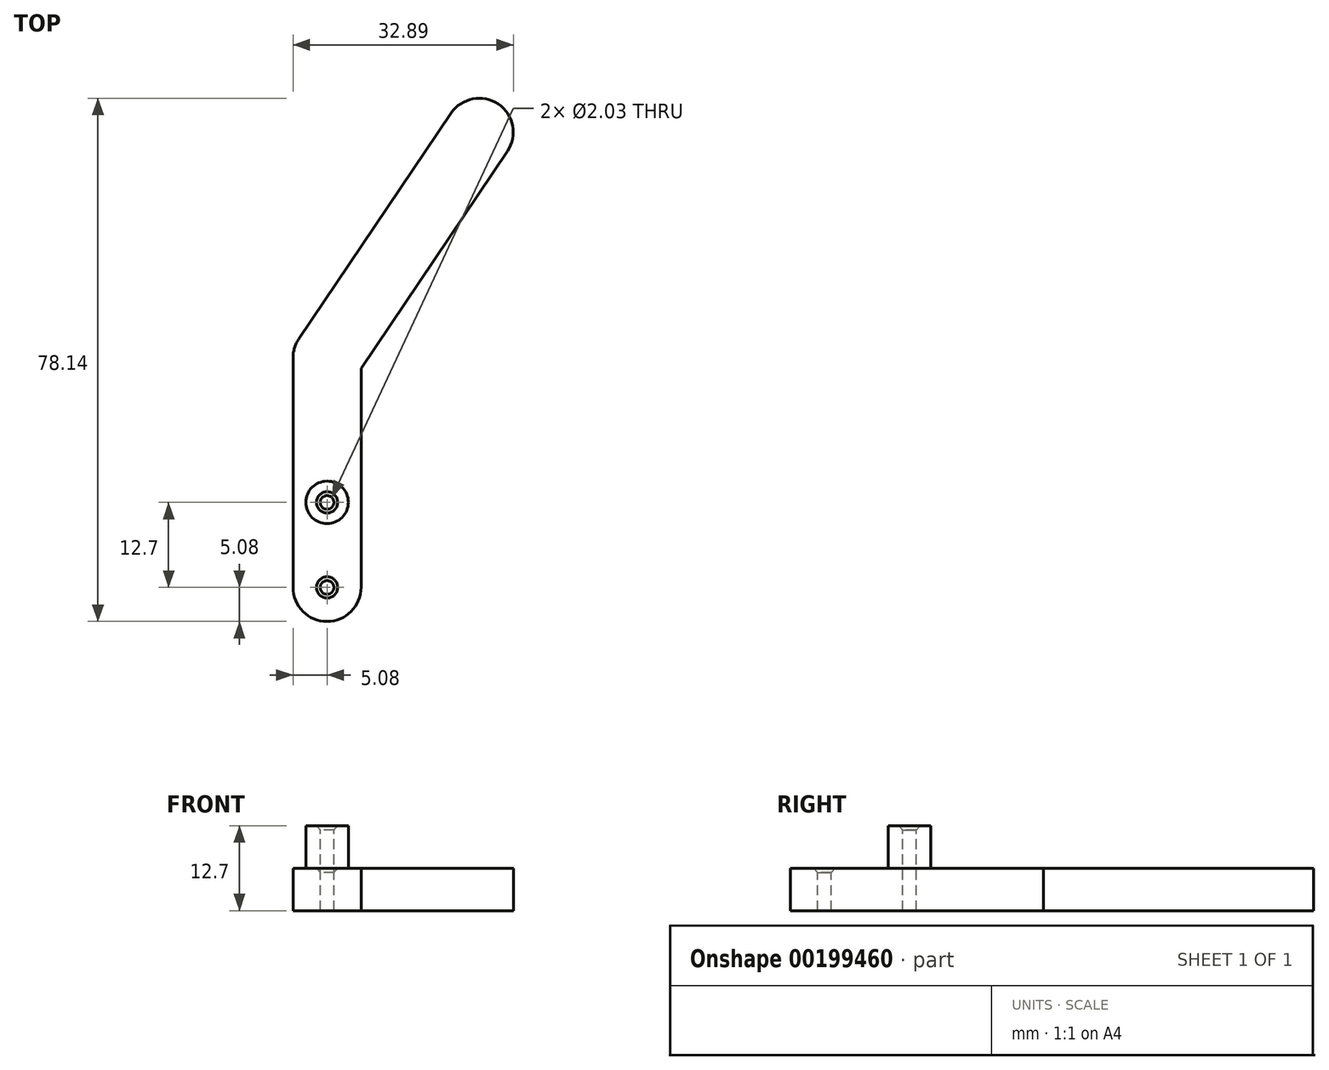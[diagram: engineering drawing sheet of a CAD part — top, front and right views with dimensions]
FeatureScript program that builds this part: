
annotation { "Feature Type Name" : "Feature", "Feature Type Description" : "" }
export const myFeature = defineFeature(function(context is Context, id is Id, definition is map)
    precondition{}
    {
        {
            var Q0;
            Q0=qCreatedBy(makeId("Top.planeOp"),FACE);
            var sketch = newSketch(context, id + "F0", { "sketchPlane" : qUnion([Q0])});
            skLineSegment(sketch, "E0", {"start": v(0, 0) * mm, "end": v(0, 12.7) * mm});
            skLineSegment(sketch, "E1", {"start": v(0, 12.7) * mm, "end": v(0, 34.3) * mm});
            skLineSegment(sketch, "E2", {"start": v(0, 34.3) * mm, "end": v(22.73, 67.98) * mm});
            skArc(sketch, "E3.0.startCap", {"start": v(4.21, 31.45) * mm, "mid": v(-2.84, 30.08) * mm, "end": v(-4.21, 37.13) * mm});
            skArc(sketch, "E3.0.endCap", {"start": v(18.51, 70.82) * mm, "mid": v(25.57, 72.2) * mm, "end": v(26.94, 65.14) * mm});
            skLineSegment(sketch, "E3.0.left", {"start": v(-4.21, 37.13) * mm, "end": v(18.51, 70.82) * mm});
            skLineSegment(sketch, "E3.0.right", {"start": v(4.21, 31.45) * mm, "end": v(26.94, 65.14) * mm});
            skArc(sketch, "E3.1.startCap", {"start": v(5.08, 12.7) * mm, "mid": v(0, 7.62) * mm, "end": v(-5.08, 12.7) * mm});
            skArc(sketch, "E3.1.endCap", {"start": v(-5.08, 34.3) * mm, "mid": v(0, 39.37) * mm, "end": v(5.08, 34.3) * mm});
            skLineSegment(sketch, "E3.1.left", {"start": v(-5.08, 12.7) * mm, "end": v(-5.08, 34.3) * mm});
            skLineSegment(sketch, "E3.1.right", {"start": v(5.08, 12.7) * mm, "end": v(5.08, 34.3) * mm});
            skArc(sketch, "E3.2.startCap", {"start": v(5.08, 0) * mm, "mid": v(0, -5.08) * mm, "end": v(-5.08, 0) * mm});
            skArc(sketch, "E3.2.endCap", {"start": v(-5.08, 12.7) * mm, "mid": v(0, 17.78) * mm, "end": v(5.08, 12.7) * mm});
            skLineSegment(sketch, "E3.2.left", {"start": v(-5.08, 0) * mm, "end": v(-5.08, 12.7) * mm});
            skLineSegment(sketch, "E3.2.right", {"start": v(5.08, 0) * mm, "end": v(5.08, 12.7) * mm});
            skSolve(sketch);
        }
        {
            var Q0;
            Q0 = qSketchRegion(id + "F0", true);
            extrude(context, id + "F1", {"entities" : qUnion([Q0]), "depth" : 6.35 * mm});
        }
        {
            var Q0;
            Q0=makeQuery(id+"F1.opExtrude","CAP_FACE",FACE,{"disambiguationData":[OSD([sQuery(id+"F0.wireOp",EDGE,"E3.0.endCap"),sQuery(id+"F0.wireOp",EDGE,"E3.0.left"),sQuery(id+"F0.wireOp",EDGE,"E3.0.right"),sQuery(id+"F0.wireOp",EDGE,"E3.1.endCap"),sQuery(id+"F0.wireOp",EDGE,"E3.1.left"),sQuery(id+"F0.wireOp",EDGE,"E3.1.right"),sQuery(id+"F0.wireOp",EDGE,"E3.2.startCap"),sQuery(id+"F0.wireOp",EDGE,"E3.2.left"),sQuery(id+"F0.wireOp",EDGE,"E3.2.right")])],"isStart":false});
            var sketch = newSketch(context, id + "F2", { "sketchPlane" : qUnion([Q0])});
            skCircle(sketch, "E4", {"center": v(0, 12.7) * mm, "radius": 3.18 * mm});
            skSolve(sketch);
        }
        {
            var Q0;
            Q0=makeQuery(id+"F2.imprint","IMPRINT",FACE,{"disambiguationData":[TD([[makeQuery(id+"F2.imprint","IMPRINT",EDGE,{"derivedFrom":sQuery(id+"F2.wireOp",EDGE,"E4")}),1.0]])]});
            extrude(context, id + "F3", {"entities" : qUnion([Q0]), "operationType" : NewBodyOperationType.ADD, "depth" : 6.35 * mm});
        }
        {
            var Q0;
            Q0=makeQuery(id+"F3.opExtrude","CAP_FACE",FACE,{"disambiguationData":[OSD([sQuery(id+"F2.wireOp",EDGE,"E4")])],"isStart":false});
            var sketch = newSketch(context, id + "F4", { "sketchPlane" : qUnion([Q0])});
            skPoint(sketch, "E5", {"position": v(0, 12.7) * mm});
            skSolve(sketch);
        }
        {
            var Q0;
            Q0=sQuery(id+"F4.wireOp",VERTEX,"E5");
            var Q1;
            Q1=makeQuery(id+"F1.opExtrude","SWEPT_BODY",BODY,{"disambiguationData":[OSD([sQuery(id+"F0.wireOp",EDGE,"E3.0.endCap"),sQuery(id+"F0.wireOp",EDGE,"E3.0.left"),sQuery(id+"F0.wireOp",EDGE,"E3.0.right"),sQuery(id+"F0.wireOp",EDGE,"E3.1.endCap"),sQuery(id+"F0.wireOp",EDGE,"E3.1.left"),sQuery(id+"F0.wireOp",EDGE,"E3.1.right"),sQuery(id+"F0.wireOp",EDGE,"E3.2.startCap"),sQuery(id+"F0.wireOp",EDGE,"E3.2.left"),sQuery(id+"F0.wireOp",EDGE,"E3.2.right")])]});
            hole(context, id + "F5", {"style" : HoleStyle.C_SINK, "endStyle" : HoleEndStyle.THROUGH, "holeDiameter" : 2.03 * mm, "cSinkDiameter" : 3.17 * mm, "cSinkAngle" : 82 * degree, "locations" : qUnion([Q0]), "scope" : qUnion([Q1]), "isTappedThrough" : true});
        }
        {
            var Q0;
            Q0=makeQuery(id+"F2.imprint","IMPRINT",FACE,{"disambiguationData":[TD([[makeQuery(id+"F2.imprint","IMPRINT",EDGE,{"derivedFrom":sQuery(id+"F2.wireOp",EDGE,"E4")}),-1.0]])]});
            var sketch = newSketch(context, id + "F6", { "sketchPlane" : qUnion([Q0])});
            skPoint(sketch, "E6", {"position": v(0, 0) * mm});
            skSolve(sketch);
        }
        {
            var Q0;
            Q0=sQuery(id+"F6.wireOp",VERTEX,"E6");
            var Q1;
            Q1=makeQuery(id+"F1.opExtrude","SWEPT_BODY",BODY,{"disambiguationData":[OSD([sQuery(id+"F0.wireOp",EDGE,"E3.0.endCap"),sQuery(id+"F0.wireOp",EDGE,"E3.0.left"),sQuery(id+"F0.wireOp",EDGE,"E3.0.right"),sQuery(id+"F0.wireOp",EDGE,"E3.1.endCap"),sQuery(id+"F0.wireOp",EDGE,"E3.1.left"),sQuery(id+"F0.wireOp",EDGE,"E3.1.right"),sQuery(id+"F0.wireOp",EDGE,"E3.2.startCap"),sQuery(id+"F0.wireOp",EDGE,"E3.2.left"),sQuery(id+"F0.wireOp",EDGE,"E3.2.right")])]});
            hole(context, id + "F7", {"style" : HoleStyle.C_SINK, "endStyle" : HoleEndStyle.THROUGH, "holeDiameter" : 2.03 * mm, "cSinkDiameter" : 3.17 * mm, "cSinkAngle" : 82 * degree, "locations" : qUnion([Q0]), "scope" : qUnion([Q1]), "isTappedThrough" : true});
        }
    });
